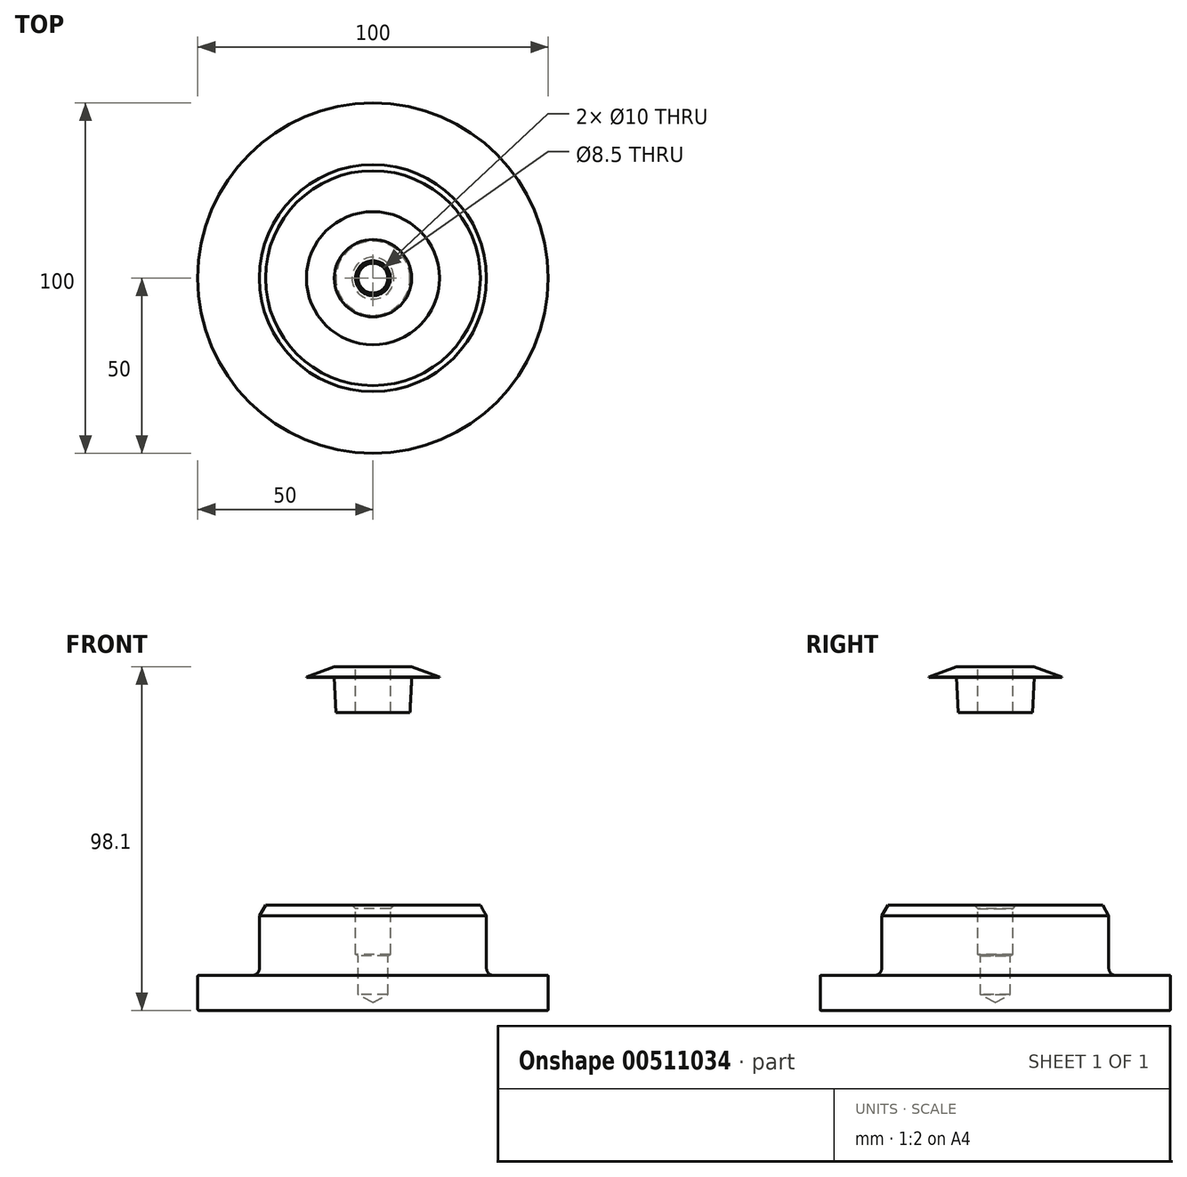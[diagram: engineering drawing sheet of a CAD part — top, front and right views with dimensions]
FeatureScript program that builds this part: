
annotation { "Feature Type Name" : "Feature", "Feature Type Description" : "" }
export const myFeature = defineFeature(function(context is Context, id is Id, definition is map)
    precondition{}
    {
        {
            var Q0;
            Q0=qCreatedBy(makeId("Front.planeOp"),FACE);
            var sketch = newSketch(context, id + "F0", { "sketchPlane" : qUnion([Q0])});
            skLineSegment(sketch, "E0", {"start": v(0, 65.73) * mm, "end": v(0, -65.73) * mm});
            skLineSegment(sketch, "E1", {"start": v(0, 0) * mm, "end": v(49.8, 0) * mm});
            skPoint(sketch, "E1.endSnap0", {"position": v(0, 0) * mm});
            skLineSegment(sketch, "E2", {"start": v(50, 0.2) * mm, "end": v(50, 9.8) * mm});
            skLineSegment(sketch, "E3", {"start": v(49.8, 10) * mm, "end": v(34.4, 10) * mm});
            skLineSegment(sketch, "E4", {"start": v(32.4, 12) * mm, "end": v(32.4, 27.01) * mm});
            skLineSegment(sketch, "E5", {"start": v(30.68, 30.01) * mm, "end": v(6, 30.01) * mm});
            skLineSegment(sketch, "E6", {"start": v(5, 85.1) * mm, "end": v(10.58, 85.1) * mm});
            skLineSegment(sketch, "E7", {"start": v(10.58, 85.1) * mm, "end": v(11.1, 95.1) * mm});
            skLineSegment(sketch, "E8", {"start": v(11.1, 95.1) * mm, "end": v(19, 95.1) * mm});
            skLineSegment(sketch, "E9", {"start": v(19, 95.1) * mm, "end": v(19, 95.2) * mm});
            skLineSegment(sketch, "E10", {"start": v(19, 95.2) * mm, "end": v(11.03, 98.1) * mm});
            skLineSegment(sketch, "E11", {"start": v(11.03, 98.1) * mm, "end": v(5, 98.1) * mm});
            skLineSegment(sketch, "E12", {"start": v(5, 98.1) * mm, "end": v(5, 85.1) * mm});
            skLineSegment(sketch, "E13", {"start": v(32.5, 75.05) * mm, "end": v(32.51, 25.01) * mm});
            skLineSegment(sketch, "E14", {"start": v(32.5, 25.01) * mm, "end": v(36.52, 10.05) * mm});
            skLineSegment(sketch, "E15", {"start": v(36.52, 10.05) * mm, "end": v(47.32, 10.05) * mm});
            skLineSegment(sketch, "E16", {"start": v(47.32, 10.05) * mm, "end": v(50, 20.05) * mm});
            skLineSegment(sketch, "E17", {"start": v(50, 20.05) * mm, "end": v(50, 95.05) * mm});
            skLineSegment(sketch, "E18", {"start": v(50, 95.05) * mm, "end": v(11.2, 95.05) * mm});
            skLineSegment(sketch, "E19", {"start": v(11.2, 95.05) * mm, "end": v(11.2, 75.05) * mm});
            skLineSegment(sketch, "E20", {"start": v(11.2, 75.05) * mm, "end": v(32.5, 75.05) * mm});
            skLineSegment(sketch, "E21", {"start": v(32.4, 27.01) * mm, "end": v(30.68, 30.01) * mm});
            skPoint(sketch, "E22.visualSharp", {"position": v(32.4, 10) * mm});
            skArc(sketch, "E22.filletArc", {"start": v(32.4, 12) * mm, "mid": v(33, 10.59) * mm, "end": v(34.4, 10) * mm});
            skPoint(sketch, "E23.visualSharp", {"position": v(50, 10) * mm});
            skArc(sketch, "E23.filletArc", {"start": v(50, 9.8) * mm, "mid": v(49.94, 9.94) * mm, "end": v(49.8, 10) * mm});
            skPoint(sketch, "E24.visualSharp", {"position": v(50, 0) * mm});
            skArc(sketch, "E24.filletArc", {"start": v(49.8, 0) * mm, "mid": v(49.94, 0.06) * mm, "end": v(50, 0.2) * mm});
            skLineSegment(sketch, "E25", {"start": v(5, 29) * mm, "end": v(5, 16) * mm});
            skLineSegment(sketch, "E26", {"start": v(5, 16) * mm, "end": v(4.25, 15.6) * mm});
            skLineSegment(sketch, "E27", {"start": v(4.25, 15.6) * mm, "end": v(4.25, 4.5) * mm});
            skLineSegment(sketch, "E28", {"start": v(4.25, 4.5) * mm, "end": v(0, 2.24) * mm});
            skLineSegment(sketch, "E29", {"start": v(6, 30) * mm, "end": v(5, 29) * mm});
            skPoint(sketch, "E30.trimOffspring.end.orphan", {"position": v(0, 30.01) * mm});
            skSolve(sketch);
        }
        {
            var Q0;
            {var subQ0=sQuery(id+"F0.wireOp",EDGE,"E1");Q0=makeQuery(id+"F0.imprint","IMPRINT",FACE,{"disambiguationData":[TD([[makeQuery(id+"F0.imprint","IMPRINT",EDGE,{"derivedFrom":subQ0}),1.0]])]});}
            var Q1;
            {var subQ0=sQuery(id+"F0.wireOp",EDGE,"E6");Q1=makeQuery(id+"F0.imprint","IMPRINT",FACE,{"disambiguationData":[TD([[makeQuery(id+"F0.imprint","IMPRINT",EDGE,{"derivedFrom":subQ0}),1.0]])]});}
            var Q2;
            Q2=sQuery(id+"F0.wireOp",EDGE,"E4");
            var Q3;
            Q3=sQuery(id+"F0.wireOp",EDGE,"E5");
            var Q4;
            Q4=sQuery(id+"F0.wireOp",EDGE,"E3");
            var Q5;
            Q5=sQuery(id+"F0.wireOp",EDGE,"E2");
            var Q6;
            Q6=sQuery(id+"F0.wireOp",EDGE,"E1");
            var Q7;
            Q7=sQuery(id+"F0.wireOp",EDGE,"E0");
            revolve(context, id + "F1", {"entities" : qUnion([Q0, Q1]), "surfaceEntities" : qUnion([Q2, Q3, Q4, Q5, Q6]), "axis" : qUnion([Q7]), "revolveType" : RevolveType.FULL});
        }
    });
